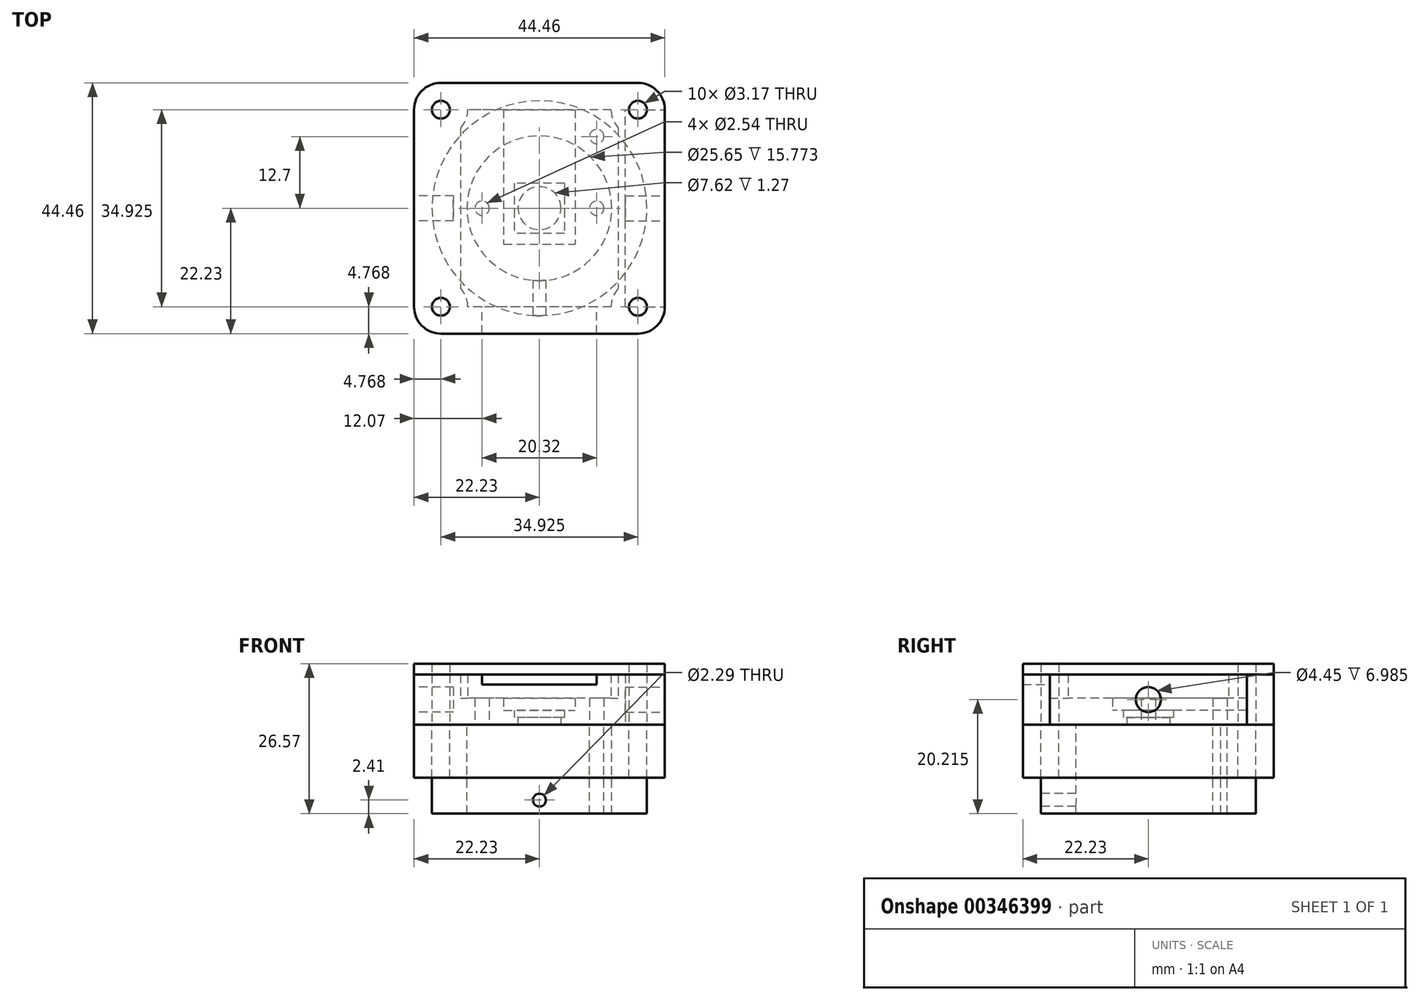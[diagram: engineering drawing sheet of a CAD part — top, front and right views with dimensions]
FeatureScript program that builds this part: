
annotation { "Feature Type Name" : "Feature", "Feature Type Description" : "" }
export const myFeature = defineFeature(function(context is Context, id is Id, definition is map)
    precondition{}
    {
        {
            var Q0;
            Q0=qCreatedBy(makeId("Top.planeOp"),FACE);
            var sketch = newSketch(context, id + "F0", { "sketchPlane" : qUnion([Q0])});
            skCircle(sketch, "E0", {"center": v(0, 0) * mm, "radius": 3.81 * mm});
            skCircle(sketch, "E1", {"center": v(-10.16, 0) * mm, "radius": 1.27 * mm});
            skCircle(sketch, "E2.MirrorC", {"center": v(10.16, 0) * mm, "radius": 1.27 * mm});
            skCircle(sketch, "E3", {"center": v(-10.16, 12.7) * mm, "radius": 1.27 * mm});
            skCircle(sketch, "E4.MirrorC", {"center": v(10.16, 12.7) * mm, "radius": 1.27 * mm});
            skLineSegment(sketch, "E5.bottom", {"start": v(-6.35, 17.46) * mm, "end": v(6.35, 17.46) * mm});
            skLineSegment(sketch, "E5.top", {"start": v(-6.35, -6.35) * mm, "end": v(6.35, -6.35) * mm});
            skLineSegment(sketch, "E5.left", {"start": v(-6.35, 17.46) * mm, "end": v(-6.35, -6.35) * mm});
            skLineSegment(sketch, "E5.right", {"start": v(6.35, 17.46) * mm, "end": v(6.35, -6.35) * mm});
            skPoint(sketch, "E6", {"position": v(0, -6.35) * mm});
            skLineSegment(sketch, "E7.bottom", {"start": v(22.23, -22.23) * mm, "end": v(-22.23, -22.23) * mm});
            skLineSegment(sketch, "E7.top", {"start": v(22.23, 22.23) * mm, "end": v(-22.23, 22.23) * mm});
            skLineSegment(sketch, "E7.left", {"start": v(22.23, -22.23) * mm, "end": v(22.23, 22.23) * mm});
            skLineSegment(sketch, "E7.right", {"start": v(-22.23, -22.23) * mm, "end": v(-22.23, 22.23) * mm});
            skLineSegment(sketch, "E8.bottom", {"start": v(17.46, -17.46) * mm, "end": v(-17.46, -17.46) * mm});
            skLineSegment(sketch, "E8.top", {"start": v(17.46, 17.46) * mm, "end": v(-17.46, 17.46) * mm});
            skLineSegment(sketch, "E8.left", {"start": v(17.46, -17.46) * mm, "end": v(17.46, 17.46) * mm});
            skLineSegment(sketch, "E8.right", {"start": v(-17.46, -17.46) * mm, "end": v(-17.46, 17.46) * mm});
            skCircle(sketch, "E9", {"center": v(-17.46, 17.46) * mm, "radius": 1.59 * mm});
            skCircle(sketch, "E10", {"center": v(17.46, 17.46) * mm, "radius": 1.59 * mm});
            skCircle(sketch, "E11", {"center": v(17.46, -17.46) * mm, "radius": 1.59 * mm});
            skCircle(sketch, "E12", {"center": v(-17.46, -17.46) * mm, "radius": 1.59 * mm});
            skCircle(sketch, "E13", {"center": v(17.46, -17.46) * mm, "radius": 4.76 * mm});
            skCircle(sketch, "E14", {"center": v(-17.46, -17.46) * mm, "radius": 4.76 * mm});
            skCircle(sketch, "E15", {"center": v(17.46, 17.46) * mm, "radius": 4.76 * mm});
            skCircle(sketch, "E16", {"center": v(-17.46, 17.46) * mm, "radius": 4.76 * mm});
            skLineSegment(sketch, "E17", {"start": v(-10.16, -22.23) * mm, "end": v(-10.16, -17.46) * mm});
            skLineSegment(sketch, "E18", {"start": v(10.16, -22.23) * mm, "end": v(10.16, -17.46) * mm});
            skLineSegment(sketch, "E19.bottom", {"start": v(4.45, 4.45) * mm, "end": v(-4.45, 4.45) * mm});
            skLineSegment(sketch, "E19.top", {"start": v(4.45, -4.45) * mm, "end": v(-4.45, -4.45) * mm});
            skLineSegment(sketch, "E19.left", {"start": v(4.45, 4.45) * mm, "end": v(4.45, -4.44) * mm});
            skLineSegment(sketch, "E19.right", {"start": v(-4.45, 4.45) * mm, "end": v(-4.45, -4.45) * mm});
            skLineSegment(sketch, "E20", {"start": v(13.97, 14.22) * mm, "end": v(13.97, -14.22) * mm});
            skLineSegment(sketch, "E21", {"start": v(-13.97, 14.22) * mm, "end": v(-13.97, -14.22) * mm});
            skSolve(sketch);
        }
        {
            var Q0;
            Q0=makeQuery(id+"F0.imprint","IMPRINT",FACE,{"disambiguationData":[TD([[makeQuery(id+"F0.imprint","IMPRINT",EDGE,{"derivedFrom":sQuery(id+"F0.wireOp",EDGE,"E1")}),-1.0]])]});
            var Q1;
            Q1=makeQuery(id+"F0.imprint","IMPRINT",FACE,{"disambiguationData":[TD([[makeQuery(id+"F0.imprint","IMPRINT",EDGE,{"derivedFrom":sQuery(id+"F0.wireOp",EDGE,"E4.MirrorC")}),-1.0]])]});
            var Q2;
            Q2=makeQuery(id+"F0.imprint","IMPRINT",FACE,{"disambiguationData":[TD([[makeQuery(id+"F0.imprint","IMPRINT",EDGE,{"derivedFrom":sQuery(id+"F0.wireOp",EDGE,"E3")}),1.0]])]});
            extrude(context, id + "F1", {"entities" : qUnion([Q0, Q1, Q2]), "depth" : 4.7 * mm, "offsetDistance" : 25.4 * mm});
        }
        {
            var Q0;
            Q0=makeQuery(id+"F0.imprint","IMPRINT",FACE,{"disambiguationData":[TD([[makeQuery(id+"F0.imprint","IMPRINT",EDGE,{"derivedFrom":sQuery(id+"F0.wireOp",EDGE,"E5.top")}),1.0]])]});
            extrude(context, id + "F2", {"entities" : qUnion([Q0]), "operationType" : NewBodyOperationType.ADD, "depth" : 2.54 * mm, "offsetDistance" : 25.4 * mm});
        }
        {
            var Q0;
            {var subQ0=sQuery(id+"F0.wireOp",EDGE,"E13");var subQ1=sQuery(id+"F0.wireOp",EDGE,"E7.bottom");var subQ2=makeQuery(id+"F0.imprint","INTERSECT",VERTEX,{"derivedFrom":[subQ1,subQ0]});Q0=makeQuery(id+"F0.imprint","IMPRINT",FACE,{"disambiguationData":[TD([[makeQuery(id+"F0.imprint","IMPRINT",EDGE,{"disambiguationData":[TD([[subQ2,-1.0]])],"derivedFrom":subQ1}),-1.0]])]});}
            var Q1;
            {var subQ4=sQuery(id+"F0.wireOp",EDGE,"E11");var subQ5=sQuery(id+"F0.wireOp",EDGE,"E8.bottom");var subQ6=makeQuery(id+"F0.imprint","INTERSECT",VERTEX,{"derivedFrom":[subQ5,subQ4]});Q1=makeQuery(id+"F0.imprint","IMPRINT",FACE,{"disambiguationData":[TD([[makeQuery(id+"F0.imprint","IMPRINT",EDGE,{"disambiguationData":[TD([[subQ6,-1.0]])],"derivedFrom":subQ5}),1.0]])]});}
            var Q2;
            {var subQ0=sQuery(id+"F0.wireOp",EDGE,"E11");var subQ1=sQuery(id+"F0.wireOp",EDGE,"E8.bottom");var subQ2=makeQuery(id+"F0.imprint","INTERSECT",VERTEX,{"derivedFrom":[subQ1,subQ0]});Q2=makeQuery(id+"F0.imprint","IMPRINT",FACE,{"disambiguationData":[TD([[makeQuery(id+"F0.imprint","IMPRINT",EDGE,{"disambiguationData":[TD([[subQ2,-1.0]])],"derivedFrom":subQ1}),-1.0]])]});}
            var Q3;
            {var subQ0=sQuery(id+"F0.wireOp",EDGE,"E13");var subQ1=sQuery(id+"F0.wireOp",EDGE,"E7.left");var subQ2=makeQuery(id+"F0.imprint","INTERSECT",VERTEX,{"derivedFrom":[subQ1,subQ0]});Q3=makeQuery(id+"F0.imprint","IMPRINT",FACE,{"disambiguationData":[TD([[makeQuery(id+"F0.imprint","IMPRINT",EDGE,{"disambiguationData":[TD([[subQ2,-1.0]])],"derivedFrom":subQ1}),1.0]])]});}
            var Q4;
            {var subQ0=sQuery(id+"F0.wireOp",EDGE,"E10");var subQ1=sQuery(id+"F0.wireOp",EDGE,"E8.top");var subQ2=makeQuery(id+"F0.imprint","INTERSECT",VERTEX,{"derivedFrom":[subQ1,subQ0]});Q4=makeQuery(id+"F0.imprint","IMPRINT",FACE,{"disambiguationData":[TD([[makeQuery(id+"F0.imprint","IMPRINT",EDGE,{"disambiguationData":[TD([[subQ2,-1.0]])],"derivedFrom":subQ1}),1.0]])]});}
            var Q5;
            {var subQ3=sQuery(id+"F0.wireOp",EDGE,"E10");var subQ4=sQuery(id+"F0.wireOp",EDGE,"E8.top");var subQ5=makeQuery(id+"F0.imprint","INTERSECT",VERTEX,{"derivedFrom":[subQ4,subQ3]});Q5=makeQuery(id+"F0.imprint","IMPRINT",FACE,{"disambiguationData":[TD([[makeQuery(id+"F0.imprint","IMPRINT",EDGE,{"disambiguationData":[TD([[subQ5,-1.0]])],"derivedFrom":subQ4}),-1.0]])]});}
            var Q6;
            {var subQ4=sQuery(id+"F0.wireOp",EDGE,"E7.top");var subQ7=sQuery(id+"F0.wireOp",EDGE,"E15");var subQ9=makeQuery(id+"F0.imprint","INTERSECT",VERTEX,{"derivedFrom":[subQ4,subQ7]});Q6=makeQuery(id+"F0.imprint","IMPRINT",FACE,{"disambiguationData":[TD([[makeQuery(id+"F0.imprint","IMPRINT",EDGE,{"disambiguationData":[TD([[subQ9,-1.0]])],"derivedFrom":subQ4}),1.0]])]});}
            var Q7;
            {var subQ0=sQuery(id+"F0.wireOp",EDGE,"E14");var subQ1=sQuery(id+"F0.wireOp",EDGE,"E8.bottom");var subQ2=makeQuery(id+"F0.imprint","INTERSECT",VERTEX,{"derivedFrom":[subQ1,subQ0]});Q7=makeQuery(id+"F0.imprint","IMPRINT",FACE,{"disambiguationData":[TD([[makeQuery(id+"F0.imprint","IMPRINT",EDGE,{"disambiguationData":[TD([[subQ2,-1.0]])],"derivedFrom":subQ1}),-1.0]])]});}
            var Q8;
            {var subQ0=sQuery(id+"F0.wireOp",EDGE,"E14");var subQ5=sQuery(id+"F0.wireOp",EDGE,"E8.bottom");var subQ8=makeQuery(id+"F0.imprint","INTERSECT",VERTEX,{"derivedFrom":[subQ5,subQ0]});Q8=makeQuery(id+"F0.imprint","IMPRINT",FACE,{"disambiguationData":[TD([[makeQuery(id+"F0.imprint","IMPRINT",EDGE,{"disambiguationData":[TD([[subQ8,-1.0]])],"derivedFrom":subQ5}),1.0]])]});}
            var Q9;
            {var subQ0=sQuery(id+"F0.wireOp",EDGE,"E14");var subQ1=sQuery(id+"F0.wireOp",EDGE,"E7.right");var subQ2=makeQuery(id+"F0.imprint","INTERSECT",VERTEX,{"derivedFrom":[subQ1,subQ0]});Q9=makeQuery(id+"F0.imprint","IMPRINT",FACE,{"disambiguationData":[TD([[makeQuery(id+"F0.imprint","IMPRINT",EDGE,{"disambiguationData":[TD([[subQ2,-1.0]])],"derivedFrom":subQ1}),-1.0]])]});}
            var Q10;
            {var subQ0=sQuery(id+"F0.wireOp",EDGE,"E16");var subQ1=sQuery(id+"F0.wireOp",EDGE,"E8.top");var subQ2=makeQuery(id+"F0.imprint","INTERSECT",VERTEX,{"derivedFrom":[subQ1,subQ0]});Q10=makeQuery(id+"F0.imprint","IMPRINT",FACE,{"disambiguationData":[TD([[makeQuery(id+"F0.imprint","IMPRINT",EDGE,{"disambiguationData":[TD([[subQ2,-1.0]])],"derivedFrom":subQ1}),1.0]])]});}
            var Q11;
            {var subQ0=sQuery(id+"F0.wireOp",EDGE,"E16");var subQ2=sQuery(id+"F0.wireOp",EDGE,"E8.top");var subQ3=makeQuery(id+"F0.imprint","INTERSECT",VERTEX,{"derivedFrom":[subQ2,subQ0]});Q11=makeQuery(id+"F0.imprint","IMPRINT",FACE,{"disambiguationData":[TD([[makeQuery(id+"F0.imprint","IMPRINT",EDGE,{"disambiguationData":[TD([[subQ3,-1.0]])],"derivedFrom":subQ2}),-1.0]])]});}
            var Q12;
            {var subQ0=sQuery(id+"F0.wireOp",EDGE,"E17");Q12=makeQuery(id+"F0.imprint","IMPRINT",FACE,{"disambiguationData":[TD([[makeQuery(id+"F0.imprint","IMPRINT",EDGE,{"derivedFrom":subQ0}),1.0]])]});}
            var Q13;
            {var subQ5=sQuery(id+"F0.wireOp",EDGE,"E21");Q13=makeQuery(id+"F0.imprint","IMPRINT",FACE,{"disambiguationData":[TD([[makeQuery(id+"F0.imprint","IMPRINT",EDGE,{"derivedFrom":subQ5}),-1.0]])]});}
            var Q14;
            {var subQ5=sQuery(id+"F0.wireOp",EDGE,"E20");Q14=makeQuery(id+"F0.imprint","IMPRINT",FACE,{"disambiguationData":[TD([[makeQuery(id+"F0.imprint","IMPRINT",EDGE,{"derivedFrom":subQ5}),1.0]])]});}
            extrude(context, id + "F3", {"entities" : qUnion([Q0, Q1, Q2, Q3, Q4, Q5, Q6, Q7, Q8, Q9, Q10, Q11, Q12, Q13, Q14]), "operationType" : NewBodyOperationType.ADD, "depth" : 8.9 * mm, "offsetDistance" : 25.4 * mm});
        }
        {
            var Q0;
            {var subQ0=sQuery(id+"F0.wireOp",EDGE,"E17");Q0=makeQuery(id+"F0.imprint","IMPRINT",FACE,{"disambiguationData":[TD([[makeQuery(id+"F0.imprint","IMPRINT",EDGE,{"derivedFrom":subQ0}),-1.0]])]});}
            extrude(context, id + "F4", {"entities" : qUnion([Q0]), "operationType" : NewBodyOperationType.ADD, "depth" : 7.11 * mm, "offsetDistance" : 25.4 * mm});
        }
        {
            var Q0;
            Q0=makeQuery(id+"F0.imprint","IMPRINT",FACE,{"disambiguationData":[TD([[makeQuery(id+"F0.imprint","IMPRINT",EDGE,{"derivedFrom":sQuery(id+"F0.wireOp",EDGE,"E0")}),-1.0]])]});
            extrude(context, id + "F5", {"entities" : qUnion([Q0]), "operationType" : NewBodyOperationType.ADD, "depth" : 1.27 * mm, "offsetDistance" : 25.4 * mm});
        }
        {
            var Q0;
            {var subQ0=sQuery(id+"F0.wireOp",EDGE,"E16");var subQ1=sQuery(id+"F0.wireOp",EDGE,"E15");var subQ2=sQuery(id+"F0.wireOp",EDGE,"E14");var subQ3=sQuery(id+"F0.wireOp",EDGE,"E13");var subQ4=sQuery(id+"F0.wireOp",EDGE,"E8.right");var subQ5=sQuery(id+"F0.wireOp",EDGE,"E8.left");var subQ6=sQuery(id+"F0.wireOp",EDGE,"E8.top");var subQ7=sQuery(id+"F0.wireOp",EDGE,"E8.bottom");var subQ8=sQuery(id+"F0.wireOp",EDGE,"E5.right");var subQ9=sQuery(id+"F0.wireOp",EDGE,"E5.left");var subQ10=sQuery(id+"F0.wireOp",EDGE,"E5.top");var subQ11=sQuery(id+"F0.wireOp",EDGE,"E5.bottom");Q0=makeQuery(id+"F3.boolean.opBoolean","MERGE",FACE,{"derivedFrom":[makeQuery(id+"F2.boolean.opBoolean","MERGE",FACE,{"derivedFrom":[makeQuery(id+"F1.opExtrude","CAP_FACE",FACE,{"disambiguationData":[OSD([sQuery(id+"F0.wireOp",EDGE,"E1"),sQuery(id+"F0.wireOp",EDGE,"E2.MirrorC"),sQuery(id+"F0.wireOp",EDGE,"E3"),sQuery(id+"F0.wireOp",EDGE,"E4.MirrorC"),subQ11,subQ10,subQ9,subQ8,subQ7,subQ6,subQ5,subQ4,subQ3,subQ2,subQ1,subQ0])],"isStart":true}),makeQuery(id+"F2.opExtrude","CAP_FACE",FACE,{"disambiguationData":[OSD([sQuery(id+"F0.wireOp",EDGE,"E0"),subQ11,subQ10,subQ9,subQ8])],"isStart":true})]}),makeQuery(id+"F3.opExtrude","CAP_FACE",FACE,{"disambiguationData":[OSD([sQuery(id+"F0.wireOp",EDGE,"E7.bottom"),sQuery(id+"F0.wireOp",EDGE,"E7.top"),sQuery(id+"F0.wireOp",EDGE,"E7.left"),sQuery(id+"F0.wireOp",EDGE,"E7.right"),subQ7,subQ6,subQ5,subQ4,sQuery(id+"F0.wireOp",EDGE,"E9"),sQuery(id+"F0.wireOp",EDGE,"E10"),sQuery(id+"F0.wireOp",EDGE,"E11"),sQuery(id+"F0.wireOp",EDGE,"E12"),subQ3,subQ2,subQ1,subQ0])],"isStart":true})]});}
            var sketch = newSketch(context, id + "F6", { "sketchPlane" : qUnion([Q0])});
            skCircle(sketch, "E22", {"center": v(0, 0) * mm, "radius": 12.83 * mm});
            skSolve(sketch);
        }
        {
            var Q0;
            Q0=makeQuery(id+"F6.imprint","IMPRINT",FACE,{"disambiguationData":[TD([[makeQuery(id+"F6.imprint","IMPRINT",EDGE,{"derivedFrom":sQuery(id+"F6.wireOp",EDGE,"E22")}),-1.0]])]});
            extrude(context, id + "F7", {"entities" : qUnion([Q0]), "depth" : 15.77 * mm, "offsetDistance" : 25.4 * mm});
        }
        {
            var Q0;
            Q0=makeQuery(id+"F3.opExtrude","CAP_FACE",FACE,{"disambiguationData":[OSD([sQuery(id+"F0.wireOp",EDGE,"E7.bottom"),sQuery(id+"F0.wireOp",EDGE,"E7.top"),sQuery(id+"F0.wireOp",EDGE,"E7.left"),sQuery(id+"F0.wireOp",EDGE,"E7.right"),sQuery(id+"F0.wireOp",EDGE,"E8.bottom"),sQuery(id+"F0.wireOp",EDGE,"E8.top"),sQuery(id+"F0.wireOp",EDGE,"E8.left"),sQuery(id+"F0.wireOp",EDGE,"E8.right"),sQuery(id+"F0.wireOp",EDGE,"E9"),sQuery(id+"F0.wireOp",EDGE,"E10"),sQuery(id+"F0.wireOp",EDGE,"E11"),sQuery(id+"F0.wireOp",EDGE,"E12"),sQuery(id+"F0.wireOp",EDGE,"E13"),sQuery(id+"F0.wireOp",EDGE,"E14"),sQuery(id+"F0.wireOp",EDGE,"E15"),sQuery(id+"F0.wireOp",EDGE,"E16"),sQuery(id+"F0.wireOp",EDGE,"E17"),sQuery(id+"F0.wireOp",EDGE,"E18")])],"isStart":false});
            var sketch = newSketch(context, id + "F8", { "sketchPlane" : qUnion([Q0])});
            skArc(sketch, "E23.0", {"start": v(17.46, -22.23) * mm, "mid": v(20.83, -20.83) * mm, "end": v(22.23, -17.46) * mm});
            skLineSegment(sketch, "E24.0", {"start": v(22.23, -22.23) * mm, "end": v(-22.23, -22.23) * mm});
            skLineSegment(sketch, "E25.0", {"start": v(-22.23, -22.23) * mm, "end": v(-22.23, 22.23) * mm});
            skArc(sketch, "E26.0", {"start": v(-17.46, 22.23) * mm, "mid": v(-20.83, 20.83) * mm, "end": v(-22.23, 17.46) * mm});
            skArc(sketch, "E27.0", {"start": v(-22.23, -17.46) * mm, "mid": v(-20.83, -20.83) * mm, "end": v(-17.46, -22.23) * mm});
            skLineSegment(sketch, "E28.0", {"start": v(17.46, 22.23) * mm, "end": v(-17.46, 22.23) * mm});
            skArc(sketch, "E29.0", {"start": v(22.23, 17.46) * mm, "mid": v(20.83, 20.83) * mm, "end": v(17.46, 22.23) * mm});
            skLineSegment(sketch, "E30.0.0", {"start": v(22.23, -17.46) * mm, "end": v(22.23, 17.46) * mm});
            skLineSegment(sketch, "E30.0.2", {"start": v(22.23, 17.46) * mm, "end": v(22.23, -17.46) * mm});
            skCircle(sketch, "E31.0", {"center": v(-17.46, 17.46) * mm, "radius": 1.59 * mm});
            skCircle(sketch, "E32.0", {"center": v(-17.46, -17.46) * mm, "radius": 1.59 * mm});
            skCircle(sketch, "E33.0", {"center": v(17.46, -17.46) * mm, "radius": 1.59 * mm});
            skCircle(sketch, "E34.0", {"center": v(17.46, 17.46) * mm, "radius": 1.59 * mm});
            skLineSegment(sketch, "E35.0", {"start": v(10.16, -22.23) * mm, "end": v(10.16, -17.46) * mm});
            skLineSegment(sketch, "E36.0", {"start": v(-10.16, -22.23) * mm, "end": v(-10.16, -17.46) * mm});
            skLineSegment(sketch, "E37", {"start": v(10.16, -17.46) * mm, "end": v(-10.16, -17.46) * mm});
            skLineSegment(sketch, "E38.0", {"start": v(-9.78, -19.05) * mm, "end": v(-9.78, -15.88) * mm});
            skLineSegment(sketch, "E39.0", {"start": v(9.78, -19.05) * mm, "end": v(9.78, -15.88) * mm});
            skSolve(sketch);
        }
        {
            var Q0;
            {var subQ17=sQuery(id+"F8.wireOp",EDGE,"E23.0");Q0=makeQuery(id+"F8.imprint","IMPRINT",FACE,{"disambiguationData":[TD([[makeQuery(id+"F8.imprint","IMPRINT",EDGE,{"derivedFrom":subQ17}),1.0]])]});}
            var Q1;
            {var subQ1=sQuery(id+"F0.wireOp",EDGE,"E8.top");Q1=makeQuery(id+"F8.imprint","IMPRINT",FACE,{"disambiguationData":[TD([[makeQuery(id+"F8.imprint","IMPRINT",EDGE,{"derivedFrom":makeQuery(id+"F3.opExtrude","CAP_EDGE",EDGE,{"disambiguationData":[OSD([subQ1])],"isStart":false})}),1.0]])]});}
            var Q2;
            {var subQ2=sQuery(id+"F8.wireOp",EDGE,"E35.0");Q2=makeQuery(id+"F8.imprint","IMPRINT",FACE,{"disambiguationData":[TD([[makeQuery(id+"F8.imprint","IMPRINT",EDGE,{"derivedFrom":subQ2}),1.0]])]});}
            var Q3;
            {var subQ0=sQuery(id+"F8.wireOp",EDGE,"E38.0");Q3=makeQuery(id+"F8.imprint","IMPRINT",FACE,{"disambiguationData":[TD([[makeQuery(id+"F8.imprint","IMPRINT",EDGE,{"derivedFrom":subQ0}),-1.0]])]});}
            var Q4;
            {var subQ0=sQuery(id+"F8.wireOp",EDGE,"E36.0");Q4=makeQuery(id+"F8.imprint","IMPRINT",FACE,{"disambiguationData":[TD([[makeQuery(id+"F8.imprint","IMPRINT",EDGE,{"derivedFrom":subQ0}),-1.0]])]});}
            extrude(context, id + "F9", {"entities" : qUnion([Q0, Q1, Q2, Q3, Q4]), "depth" : 1.9 * mm, "offsetDistance" : 25.4 * mm});
        }
        {
            var Q0;
            Q0=makeQuery(id+"F7.opExtrude","SWEPT_FACE",FACE,{"disambiguationData":[OSD([sQuery(id+"F0.wireOp",EDGE,"E7.bottom")])]});
            var sketch = newSketch(context, id + "F10", { "sketchPlane" : qUnion([Q0])});
            skCircle(sketch, "E40", {"center": v(0, -13.36) * mm, "radius": 1.14 * mm});
            skPoint(sketch, "E40.centerSnap0", {"position": v(0, -15.77) * mm});
            skSolve(sketch);
        }
        {
            var Q0;
            Q0=makeQuery(id+"F10.imprint","IMPRINT",FACE,{"disambiguationData":[TD([[makeQuery(id+"F10.imprint","IMPRINT",EDGE,{"derivedFrom":sQuery(id+"F10.wireOp",EDGE,"E40")}),1.0]])]});
            extrude(context, id + "F11", {"entities" : qUnion([Q0]), "operationType" : NewBodyOperationType.REMOVE, "endBound" : BoundingType.UP_TO_NEXT, "oppositeDirection" : true, "depth" : 25.4 * mm, "offsetDistance" : 25.4 * mm});
        }
        {
            var Q0;
            Q0=makeQuery(id+"F7.opExtrude","CAP_FACE",FACE,{"disambiguationData":[OSD([sQuery(id+"F0.wireOp",EDGE,"E7.bottom"),sQuery(id+"F0.wireOp",EDGE,"E7.top"),sQuery(id+"F0.wireOp",EDGE,"E7.left"),sQuery(id+"F0.wireOp",EDGE,"E7.right"),sQuery(id+"F0.wireOp",EDGE,"E9"),sQuery(id+"F0.wireOp",EDGE,"E10"),sQuery(id+"F0.wireOp",EDGE,"E11"),sQuery(id+"F0.wireOp",EDGE,"E12"),sQuery(id+"F0.wireOp",EDGE,"E13"),sQuery(id+"F0.wireOp",EDGE,"E14"),sQuery(id+"F0.wireOp",EDGE,"E15"),sQuery(id+"F0.wireOp",EDGE,"E16"),sQuery(id+"F6.wireOp",EDGE,"E22")])],"isStart":false});
            var sketch = newSketch(context, id + "F12", { "sketchPlane" : qUnion([Q0])});
            skCircle(sketch, "E41", {"center": v(0, 0) * mm, "radius": 19.05 * mm});
            skSolve(sketch);
        }
        {
            var Q0;
            Q0=makeQuery(id+"F12.imprint","IMPRINT",FACE,{"disambiguationData":[TD([[makeQuery(id+"F12.imprint","IMPRINT",EDGE,{"derivedFrom":makeQuery(id+"F7.opExtrude","CAP_EDGE",EDGE,{"disambiguationData":[OSD([sQuery(id+"F0.wireOp",EDGE,"E10")])],"isStart":false})}),1.0]])]});
            var Q1;
            Q1=makeQuery(id+"F12.imprint","IMPRINT",FACE,{"disambiguationData":[TD([[makeQuery(id+"F12.imprint","IMPRINT",EDGE,{"derivedFrom":makeQuery(id+"F7.opExtrude","CAP_EDGE",EDGE,{"disambiguationData":[OSD([sQuery(id+"F0.wireOp",EDGE,"E9")])],"isStart":false})}),1.0]])]});
            var Q2;
            Q2=makeQuery(id+"F12.imprint","IMPRINT",FACE,{"disambiguationData":[TD([[makeQuery(id+"F12.imprint","IMPRINT",EDGE,{"derivedFrom":makeQuery(id+"F7.opExtrude","CAP_EDGE",EDGE,{"disambiguationData":[OSD([sQuery(id+"F0.wireOp",EDGE,"E12")])],"isStart":false})}),1.0]])]});
            var Q3;
            Q3=makeQuery(id+"F12.imprint","IMPRINT",FACE,{"disambiguationData":[TD([[makeQuery(id+"F12.imprint","IMPRINT",EDGE,{"derivedFrom":makeQuery(id+"F7.opExtrude","CAP_EDGE",EDGE,{"disambiguationData":[OSD([sQuery(id+"F0.wireOp",EDGE,"E11")])],"isStart":false})}),1.0]])]});
            extrude(context, id + "F13", {"entities" : qUnion([Q0, Q1, Q2, Q3]), "operationType" : NewBodyOperationType.REMOVE, "oppositeDirection" : true, "depth" : 6.35 * mm, "offsetDistance" : 25.4 * mm});
        }
        {
            var Q0;
            Q0=makeQuery(id+"F3.opExtrude","SWEPT_FACE",FACE,{"disambiguationData":[OSD([sQuery(id+"F0.wireOp",EDGE,"E7.right")])]});
            var sketch = newSketch(context, id + "F14", { "sketchPlane" : qUnion([Q0])});
            skCircle(sketch, "E42", {"center": v(0, 4.45) * mm, "radius": 2.22 * mm});
            skPoint(sketch, "E42.centerSnap0", {"position": v(17.46, 4.45) * mm});
            skSolve(sketch);
        }
        {
            var Q0;
            Q0=makeQuery(id+"F14.imprint","IMPRINT",FACE,{"disambiguationData":[TD([[makeQuery(id+"F14.imprint","IMPRINT",EDGE,{"derivedFrom":sQuery(id+"F14.wireOp",EDGE,"E42")}),1.0]])]});
            extrude(context, id + "F15", {"entities" : qUnion([Q0]), "operationType" : NewBodyOperationType.REMOVE, "oppositeDirection" : true, "depth" : 7 * mm, "offsetDistance" : 25.4 * mm});
        }
        {
            var Q0;
            Q0=makeQuery(id+"F3.opExtrude","SWEPT_FACE",FACE,{"disambiguationData":[OSD([sQuery(id+"F0.wireOp",EDGE,"E7.left")])]});
            var sketch = newSketch(context, id + "F16", { "sketchPlane" : qUnion([Q0])});
            skCircle(sketch, "E43.0", {"center": v(0, 4.45) * mm, "radius": 2.22 * mm});
            skSolve(sketch);
        }
        {
            var Q0;
            Q0=makeQuery(id+"F16.imprint","IMPRINT",FACE,{"disambiguationData":[TD([[makeQuery(id+"F16.imprint","IMPRINT",EDGE,{"derivedFrom":sQuery(id+"F16.wireOp",EDGE,"E43.0")}),-1.0]])]});
            extrude(context, id + "F17", {"entities" : qUnion([Q0]), "operationType" : NewBodyOperationType.REMOVE, "oppositeDirection" : true, "depth" : 7 * mm, "offsetDistance" : 25.4 * mm});
        }
    });
